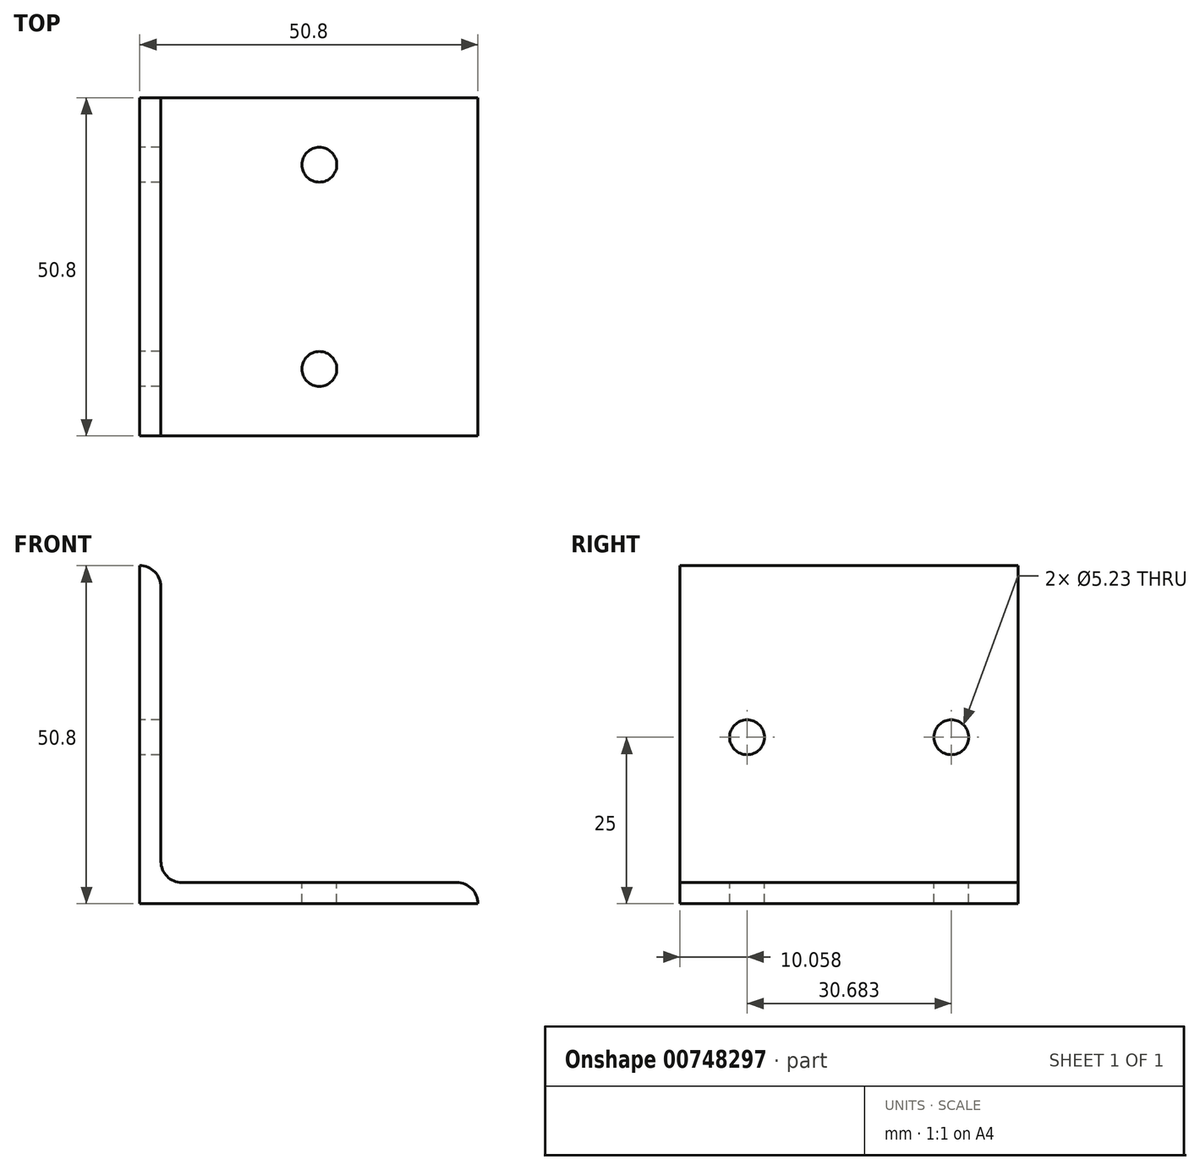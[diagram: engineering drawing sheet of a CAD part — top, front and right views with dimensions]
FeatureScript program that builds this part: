
annotation { "Feature Type Name" : "Feature", "Feature Type Description" : "" }
export const myFeature = defineFeature(function(context is Context, id is Id, definition is map)
    precondition{}
    {
        {
            var Q0;
            Q0=qCreatedBy(makeId("Front.planeOp"),FACE);
            var sketch = newSketch(context, id + "F0", { "sketchPlane" : qUnion([Q0])});
            skLineSegment(sketch, "E0", {"start": v(0, 0) * mm, "end": v(-50.8, 0) * mm});
            skLineSegment(sketch, "E1", {"start": v(-50.8, 0) * mm, "end": v(-50.8, 50.8) * mm});
            skLineSegment(sketch, "E2", {"start": v(-50.8, 50.8) * mm, "end": v(-50.8, 50.8) * mm});
            skLineSegment(sketch, "E3", {"start": v(-47.63, 47.63) * mm, "end": v(-47.63, 6.35) * mm});
            skLineSegment(sketch, "E4", {"start": v(-44.45, 3.18) * mm, "end": v(-3.18, 3.18) * mm});
            skLineSegment(sketch, "E5", {"start": v(0, 0) * mm, "end": v(0, 0) * mm});
            skPoint(sketch, "E6.visualSharp", {"position": v(-47.63, 3.18) * mm});
            skArc(sketch, "E6.filletArc", {"start": v(-47.63, 6.35) * mm, "mid": v(-46.7, 4.1) * mm, "end": v(-44.45, 3.18) * mm});
            skPoint(sketch, "E7.visualSharp", {"position": v(-47.63, 50.8) * mm});
            skArc(sketch, "E7.filletArc", {"start": v(-47.63, 47.63) * mm, "mid": v(-48.55, 49.87) * mm, "end": v(-50.8, 50.8) * mm});
            skPoint(sketch, "E8.visualSharp", {"position": v(0, 3.18) * mm});
            skArc(sketch, "E8.filletArc", {"start": v(0, 0) * mm, "mid": v(-0.93, 2.25) * mm, "end": v(-3.18, 3.18) * mm});
            skSolve(sketch);
        }
        {
            var Q0;
            Q0=qSketchRegion(id+"F0",true);
            extrude(context, id + "F1", {"entities" : qUnion([Q0]), "depth" : 50.8 * mm, "offsetDistance" : 25.4 * mm});
        }
        {
            var Q0;
            Q0=makeQuery(id+"F1.opExtrude","SWEPT_FACE",FACE,{"disambiguationData":[OSD([sQuery(id+"F0.wireOp",EDGE,"E4")])]});
            var sketch = newSketch(context, id + "F2", { "sketchPlane" : qUnion([Q0])});
            skLineSegment(sketch, "E9", {"start": v(-23.81, -50.8) * mm, "end": v(-23.81, 0) * mm, "construction": true});
            skLineSegment(sketch, "E10", {"start": v(-3.18, -40.74) * mm, "end": v(-44.45, -40.74) * mm, "construction": true});
            skCircle(sketch, "E11", {"center": v(-23.81, -40.74) * mm, "radius": 2.62 * mm});
            skLineSegment(sketch, "E12", {"start": v(-44.45, -10.06) * mm, "end": v(-3.18, -10.06) * mm, "construction": true});
            skCircle(sketch, "E13", {"center": v(-23.81, -10.06) * mm, "radius": 2.62 * mm});
            skLineSegment(sketch, "E14", {"start": v(-44.45, -25.4) * mm, "end": v(-3.18, -25.4) * mm, "construction": true});
            skSolve(sketch);
        }
        {
            var Q0;
            Q0=qSketchRegion(id+"F2",true);
            extrude(context, id + "F3", {"entities" : qUnion([Q0]), "operationType" : NewBodyOperationType.REMOVE, "endBound" : BoundingType.THROUGH_ALL, "oppositeDirection" : true, "depth" : 25.4 * mm, "offsetDistance" : 25.4 * mm});
        }
        {
            var Q0;
            Q0=makeQuery(id+"F1.opExtrude","SWEPT_FACE",FACE,{"disambiguationData":[OSD([sQuery(id+"F0.wireOp",EDGE,"E1")])]});
            var sketch = newSketch(context, id + "F4", { "sketchPlane" : qUnion([Q0])});
            skLineSegment(sketch, "E15", {"start": v(0, 25) * mm, "end": v(50.8, 25) * mm, "construction": true});
            skLineSegment(sketch, "E16", {"start": v(25.4, 50.8) * mm, "end": v(25.4, 0) * mm, "construction": true});
            skLineSegment(sketch, "E17", {"start": v(25.4, 0) * mm, "end": v(23.18, 0.53) * mm, "construction": true});
            skLineSegment(sketch, "E18", {"start": v(10.06, 50.8) * mm, "end": v(10.06, 0) * mm, "construction": true});
            skLineSegment(sketch, "E19", {"start": v(10.06, 0) * mm, "end": v(7.88, -0.15) * mm, "construction": true});
            skLineSegment(sketch, "E20", {"start": v(40.74, 50.8) * mm, "end": v(40.74, 0) * mm, "construction": true});
            skCircle(sketch, "E21", {"center": v(10.06, 25) * mm, "radius": 2.62 * mm});
            skCircle(sketch, "E22", {"center": v(40.74, 25) * mm, "radius": 2.62 * mm});
            skSolve(sketch);
        }
        {
            var Q0;
            Q0 = qSketchRegion(id + "F4", true);
            extrude(context, id + "F5", {"entities" : qUnion([Q0]), "operationType" : NewBodyOperationType.REMOVE, "endBound" : BoundingType.THROUGH_ALL, "oppositeDirection" : true, "depth" : 25.4 * mm, "offsetDistance" : 25.4 * mm});
        }
    });
